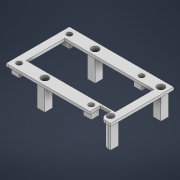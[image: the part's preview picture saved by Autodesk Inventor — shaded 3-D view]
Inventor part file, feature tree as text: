
AUTODESK INVENTOR PART (.ipt)
format: ipt  version: 2021 (Build 250183000, 183)  size: 321,536 bytes
history: native  units: mm
features: extrude x12, sketch x11, fillet x1
ambient origin geometry x8: Origin, YZ Plane, XZ Plane, XY Plane, X Axis, Y Axis, Z Axis, Center Point
bodies: Volumenkörper1 (feature_tree)
feature tree (24):
  sketch  "Skizze1"  dims[d0=57.0mm d1=45.0mm]
  extrude  "Extrusion1"  Depth=45.0mm
  extrude  "Extrusion2"  Depth=3.2mm
  extrude  "Extrusion3"  Depth=3.2mm
  extrude  "Extrusion4"  Depth=39.0mm
  extrude  "Extrusion5"  Depth=51.0mm
  extrude  "Extrusion6"  Depth=39.0mm
  extrude  "Extrusion7"  Depth=3.0mm
  extrude  "Extrusion8"  Depth=6.0mm
  extrude  "Extrusion9"  Depth=8.0mm
  sketch  "Skizze7"  dims[d13=3.0mm d14=25.5mm]
  extrude  "Extrusion10"  Depth=6.0mm
  extrude  "Extrusion11"  Depth=6.0mm
  extrude  "Extrusion12"  Depth=6.0mm
  fillet  "Rundung1"  Radius=6.0mm
  sketch  "Skizze2"  dims[d2=3.2mm d3=3.2mm]
  sketch  "Skizze3"  dims[d4=3.2mm d5=3.2mm]
  sketch  "Skizze4"  dims[d6=39.0mm d7=19.5mm]
  sketch  "Skizze5"  dims[d8=51.0mm d9=51.0mm]
  sketch  "Skizze6"  dims[d10=39.0mm d11=19.5mm]
  sketch  "Skizze8"  dims[d15=6.0mm d16=6.0mm]
  sketch  "Skizze9"  dims[d17=0.0mm d18=8.0mm]
  sketch  "Skizze10"  dims[d19=6.0mm d20=6.0mm]
  sketch  "Skizze11"  dims[d21=6.0mm d22=6.0mm d23=6.0mm d24=6.0mm d25=2.0mm d26=0.0mm d27=23.0mm d28=0.0mm d29=2.0mm d30=0.0mm d31=20.0mm d32=0.0mm d33=4.0mm d34=4.0mm d35=39.0mm d36=19.5mm d37=18.0mm d38=18.0mm d39=4.0mm d40=4.0mm d41=3.0mm d42=3.0mm d43=56.0mm d44=56.0mm d45=6.0mm d46=6.0mm d47=6.0mm d48=6.0mm d49=6.0mm d50=6.0mm d51=15.0mm d52=6.0mm d53=6.0mm d54=15.0mm d55=5.0mm d56=0.0mm d57=6.0mm d58=0.0mm d59=3.2mm d60=3.2mm d61=3.2mm d62=3.2mm d63=3.0mm d64=3.0mm d65=5.0mm d66=0.0mm d67=69.0mm d68=30.0mm d69=4.0mm d70=0.0mm d71=0.0mm d72=5.5mm d73=63.0mm d74=6.0mm d75=0.0mm d76=2.0mm d77=0.0mm d78=2.0mm d79=0.0mm d80=5.0mm d81=5.5mm d82=5.5mm d83=2.0mm d84=0.0mm d85=2.0mm d86=0.0mm d87=4.0mm d88=0.0mm d89=4.0mm]
